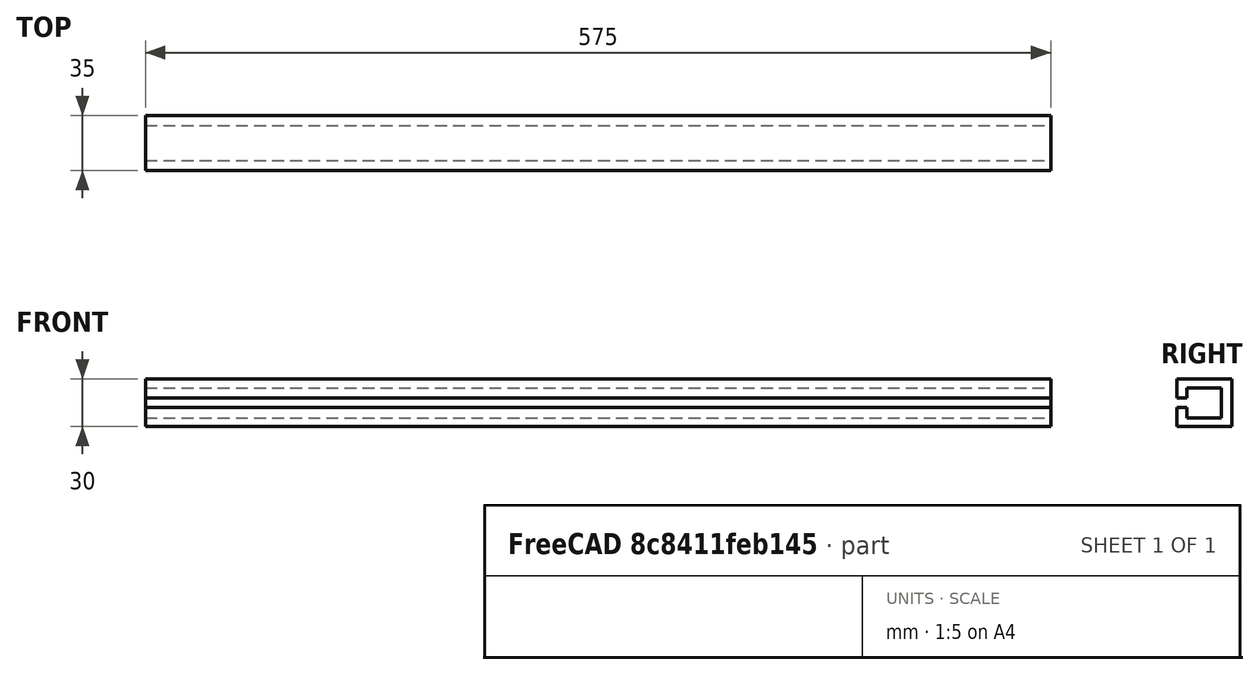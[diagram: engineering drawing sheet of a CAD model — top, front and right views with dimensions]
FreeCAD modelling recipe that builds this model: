
FCSTD DOCUMENT  (FreeCAD 0.21R33771 (Git))
Label: wellhofer-horizontal-belt-drive-cover
License: All rights reserved
LicenseURL: https://en.wikipedia.org/wiki/All_rights_reserved
objects: Sketcher::SketchObject×1, PartDesign::Pad×1, PartDesign::Body×1
note: 4 computed .brp shape members not serialized (recipe doc carries the construction recipe); baked Part::Feature solids carry a one-line shape summary decoded from their .brp

FEATURE [Sketcher::SketchObject] Sketch
  FullyConstrained = true
  MapMode = 5
  Placement = pos=(0,0,0) rot=(0.57735,0.57735,0.57735;2.0944rad)
  Support = -> [YZ_Plane]
  sketch-geometry (12):
    g0: LineSegment StartX=0 StartY=0 StartZ=0 EndX=35 EndY=0 EndZ=0
    g1: LineSegment StartX=35 StartY=0 StartZ=0 EndX=35 EndY=30 EndZ=0
    g2: LineSegment StartX=35 StartY=30 StartZ=0 EndX=0 EndY=30 EndZ=0
    g3: LineSegment StartX=0 StartY=30 StartZ=0 EndX=0 EndY=18 EndZ=0
    g4: LineSegment StartX=0 StartY=18 StartZ=0 EndX=6.5 EndY=18 EndZ=0
    g5: LineSegment StartX=6.5 StartY=18 StartZ=0 EndX=6.5 EndY=24.5 EndZ=0
    g6: LineSegment StartX=6.5 StartY=24.5 StartZ=0 EndX=28.5 EndY=24.5 EndZ=0
    g7: LineSegment StartX=28.5 StartY=5.5 StartZ=0 EndX=6.5 EndY=5.5 EndZ=0
    g8: LineSegment StartX=0 StartY=0 StartZ=0 EndX=0 EndY=12 EndZ=0
    g9: LineSegment StartX=0 StartY=12 StartZ=0 EndX=6.5 EndY=12 EndZ=0
    g10: LineSegment StartX=6.5 StartY=12 StartZ=0 EndX=6.5 EndY=5.5 EndZ=0
    g11: LineSegment StartX=28.5 StartY=24.5 StartZ=0 EndX=28.5 EndY=5.5 EndZ=0
  constraints (35):
    c: Coincident(g0,g-1)
    c: PointOnObject(g0,g-1)
    c: Coincident(g1,g0)
    c: Vertical(g1)
    c: PointOnObject(g2,g-2)
    c: Horizontal(g2)
    c: Coincident(g3,g2)
    c: PointOnObject(g3,g-2)
    c: Coincident(g4,g3)
    c: Horizontal(g4)
    c: Vertical(g5)
    c: Horizontal(g6)
    c: Horizontal(g7)
    c: Coincident(g8,g0)
    c: PointOnObject(g8,g-2)
    c: Horizontal(g9)
    c: Coincident(g10,g7)
    c: DistanceX(g4,g4) = 6.5
    c: DistanceX(g9,g9) = 6.5
    c: DistanceX(g6,g6) = 22
    c: DistanceX(g7,g7) = 22
    c: Vertical(g10)
    c: DistanceX(g0,g0) = 35
    c: DistanceY(g1,g1) = 30
    c: DistanceY(g3,g3) = 12
    c: DistanceY(g8,g8) = 12
    c: DistanceY(g10,g10) = 6.5
    c: DistanceY(g5,g5) = 6.5
    c: Coincident(g6,g5)
    c: Coincident(g10,g9)
    c: Coincident(g9,g8)
    c: Coincident(g5,g4)
    c: Coincident(g2,g1)
    c: Coincident(g11,g6)
    c: Coincident(g11,g7)
FEATURE [PartDesign::Pad] Pad
  Direction = (1,-2e-16,3e-16)
  Length = 575
  Length2 = 10
  Placement = pos=(0,0,0) rot=(0.57735,0.57735,0.57735;2.0944rad)
  Profile = -> Sketch
  ReferenceAxis = -> Sketch [N_Axis]
  Type = 0
FEATURE [PartDesign::Body] Body
  Group = -> [Sketch,Pad]
  Origin = -> Origin
  Tip = -> Pad
